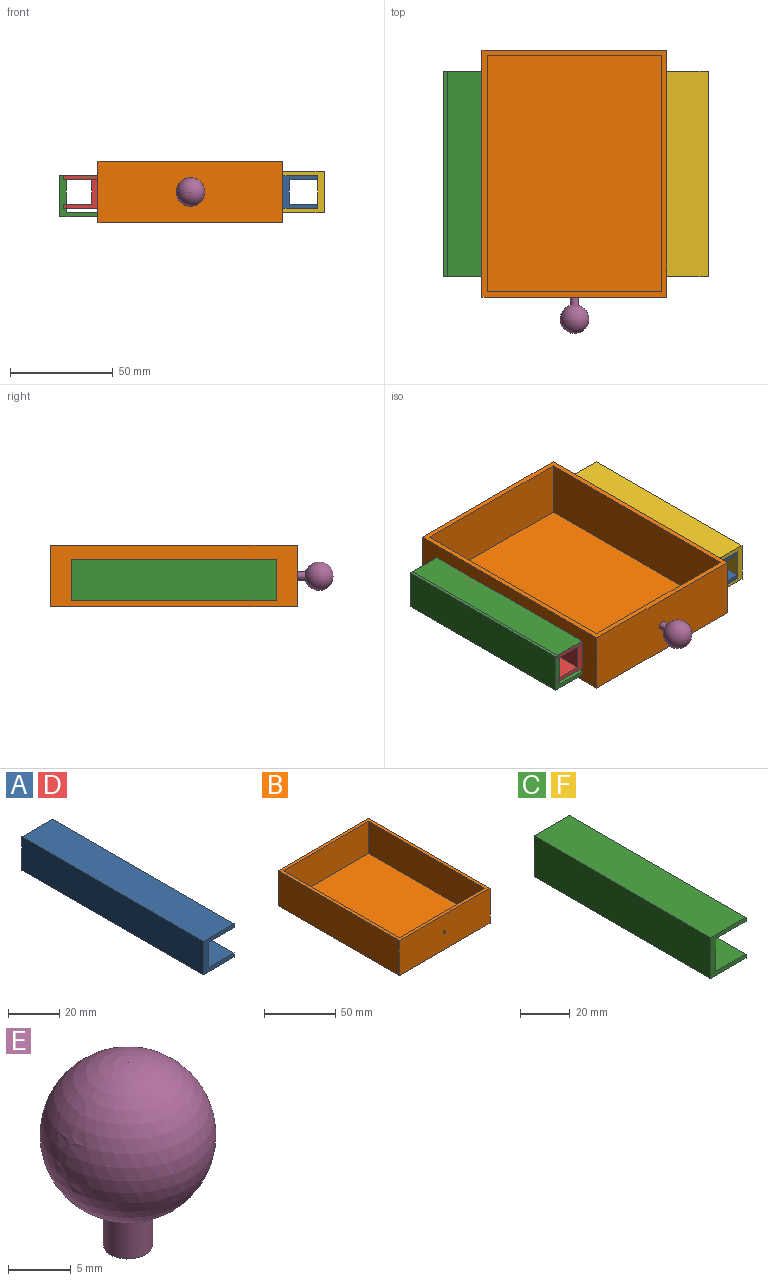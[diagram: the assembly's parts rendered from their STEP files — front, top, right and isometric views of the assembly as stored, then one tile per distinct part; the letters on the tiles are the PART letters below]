
ASSEMBLY  parts=6 mates=5
PART A: 10 faces, bbox 17x100x16 mm
  f0: plane 100x17mm, normal (0,0,-1), area 1700mm2, adj f1,f7,f8,f9
  f1: plane 100x2mm, normal (1,0,0), area 200mm2, adj f0,f2,f8,f9
  f2: plane 100x14mm, normal (0,0,1), area 1400mm2, adj f1,f3,f8,f9
  f3: plane 100x12mm, normal (1,0,0), area 1200mm2, adj f2,f4,f8,f9
  f4: plane 100x14mm, normal (0,0,-1), area 1400mm2, adj f3,f5,f8,f9
  f5: plane 100x2mm, normal (1,0,0), area 200mm2, adj f4,f6,f8,f9
  f6: plane 100x17mm, normal (0,0,1), area 1700mm2, adj f5,f7,f8,f9
  f7: plane 100x16mm, normal (-1,0,0), area 1600mm2, adj f0,f6,f8,f9
  f8: plane 17x16mm, normal (0,-1,0), area 104mm2, adj f0,f1,f2,f3,f4,f5,f6,f7
  f9: plane 17x16mm, normal (0,1,0), area 104mm2, adj f0,f1,f2,f3,f4,f5,f6,f7
PART B: 12 faces, bbox 90x120x30 mm
  f0: plane 120x90mm, normal (0,0,1), area 1025mm2, adj f1,f2,f3,f4,f6,f7,f8,f9
  f1: plane 90x30mm, normal (0,-1,0), area 2696.9mm2, adj f0,f2,f4,f5,f11
  f2: plane 120x30mm, normal (1,0,0), area 3600mm2, adj f0,f1,f3,f5
  f3: plane 90x30mm, normal (0,1,0), area 2700mm2, adj f0,f2,f4,f5
  f4: plane 120x30mm, normal (-1,0,0), area 3600mm2, adj f0,f1,f3,f5
  f5: plane 120x90mm, normal (0,0,-1), area 10800mm2, adj f1,f2,f3,f4
  f6: plane 85x27.5mm, normal (0,1,0), area 2334.4mm2, adj f0,f7,f9,f10,f11
  f7: plane 115x27.5mm, normal (-1,0,0), area 3162.5mm2, adj f0,f6,f8,f10
  f8: plane 85x27.5mm, normal (0,-1,0), area 2337.5mm2, adj f0,f7,f9,f10
  f9: plane 115x27.5mm, normal (1,0,0), area 3162.5mm2, adj f0,f6,f8,f10
  f10: plane 115x85mm, normal (0,0,1), area 9775mm2, adj f6,f7,f8,f9
  f11: cylinder r=1mm len=2.5mm, axis (0,-1,0), area 15.7mm2, adj f1,f6
PART C: 10 faces, bbox 20x100x20 mm
  f0: plane 100x20mm, normal (0,0,-1), area 2000mm2, adj f1,f7,f8,f9
  f1: plane 100x2mm, normal (1,0,0), area 200mm2, adj f0,f2,f8,f9
  f2: plane 100x17mm, normal (0,0,1), area 1700mm2, adj f1,f3,f8,f9
  f3: plane 100x16mm, normal (1,0,0), area 1600mm2, adj f2,f4,f8,f9
  f4: plane 100x17mm, normal (0,0,-1), area 1700mm2, adj f3,f5,f8,f9
  f5: plane 100x2mm, normal (1,0,0), area 200mm2, adj f4,f6,f8,f9
  f6: plane 100x20mm, normal (0,0,1), area 2000mm2, adj f5,f7,f8,f9
  f7: plane 100x20mm, normal (-1,0,0), area 2000mm2, adj f0,f6,f8,f9
  f8: plane 20x20mm, normal (0,-1,0), area 128mm2, adj f0,f1,f2,f3,f4,f5,f6,f7
  f9: plane 20x20mm, normal (0,1,0), area 128mm2, adj f0,f1,f2,f3,f4,f5,f6,f7
PART D: same geometry as A
PART E: 3 faces, bbox 14x14x17.7 mm
  f0: plane 3.92x3.92mm, normal (0,0,-1), area 12.1mm2, adj f2
  f1: sphere r=7mm, area 603.4mm2, adj f2
  f2: cylinder r=1.96mm len=3.98mm, axis (0,0,-1), area 49mm2, adj f0,f1
PART F: same geometry as C
PLACE A t=(53.5,50,15)mm
PLACE B at identity fixed
PLACE C t=(-53.5,50,13)mm
PLACE D rot(axis=(0,1,0),180deg) t=(-53.5,50,15)mm
PLACE E rot(axis=(1,0,0),90deg) t=(0,-70.7,15)mm
PLACE F rot(axis=(0,-1,0),180deg) t=(55,50,15)mm
MATE fastened E.f2 <-> B.f11  axis (0,1,0) through (0,-60,15)mm
MATE fastened B.f4 <-> D.f7  axis (-1,0,0) through (-45,0,15)mm
MATE fastened A.f7 <-> B.f2  axis (-1,0,0) through (45,0,15)mm
MATE fastened D.f0 <-> C.f6  axis (0,0,1) through (-53.5,0,23)mm
MATE fastened A.f6 <-> F.f2  axis (0,0,1) through (53.5,0,23)mm
